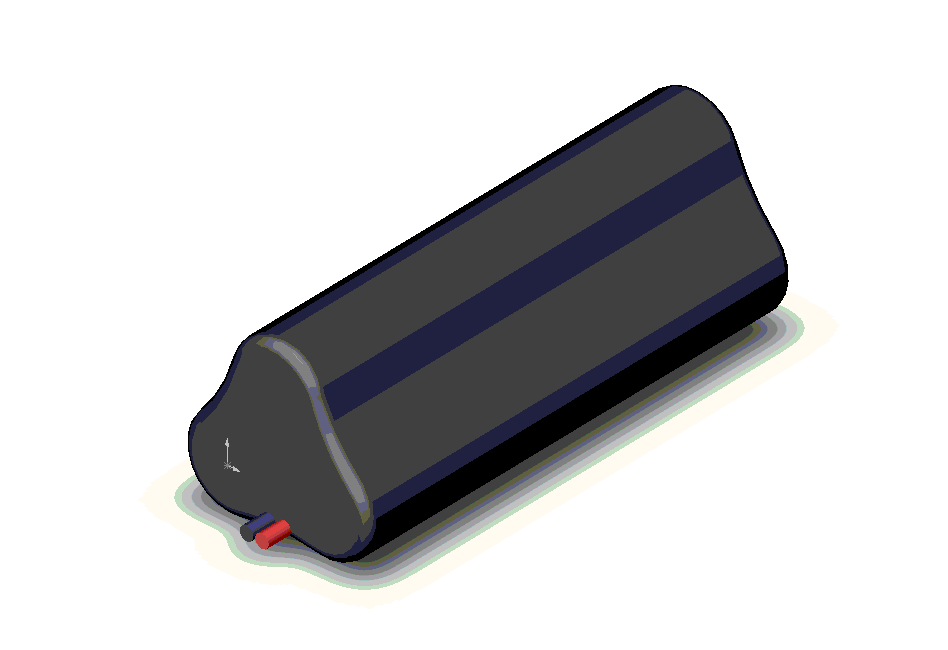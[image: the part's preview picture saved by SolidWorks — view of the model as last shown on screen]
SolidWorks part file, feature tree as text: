
SOLIDWORKS PART (.sldprt)
format: sldprt  version: not decoded by parser v0  size: 183,296 bytes
history: native  units: mm
features: sketch x3, extrude x3, fillet x1 (+8 scaffold rows collapsed)
feature tree (15):
  scaffold x8  (default folders/planes/origin — collapsed)
  sketch  "Sketch1"  dims[c1.D1=27.0mm c1.D2=27.0mm c1.D3=27.0mm c2.D2=27.0mm c2.D4=50.0mm]
  extrude  "Base-Extrude"  Depth=135mm
  fillet  "Fillet1"  Radius=3mm
  sketch  "Sketch2"  dims[D1=4.0mm D2=4.0mm D3=11.5mm D4=9.0mm]
  extrude  "Boss-Extrude1"  Depth=7mm
  sketch  "Sketch3"  dims[c1.D1=4.0mm c1.D4=4.0mm c1.D5=4.0mm c2.D1=4.0mm c2.D3=4.0mm c2.D2=~9.086083mm c3.D3=16.0mm]
  extrude  "Boss-Extrude4"  Depth=10mm
decode coverage: 7 of 7 modeling features carry decoded parameters
note: ~ marks probable driven/reference dimensions
note: suppression state not decoded; provenance and decode notes live in map.json
